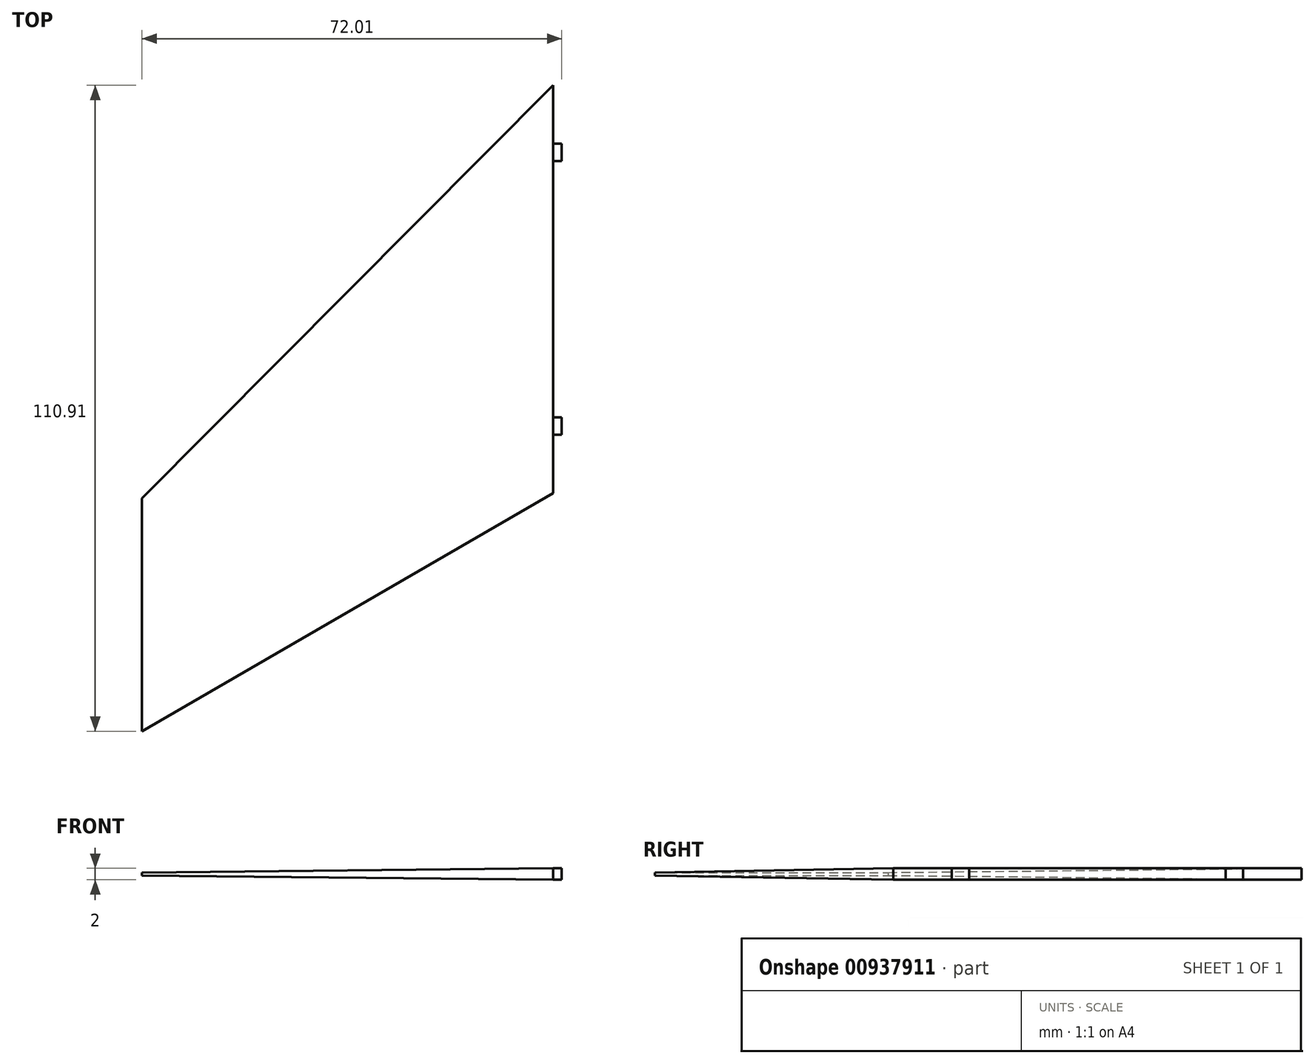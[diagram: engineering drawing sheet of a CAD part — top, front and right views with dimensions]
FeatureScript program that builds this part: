
annotation { "Feature Type Name" : "Feature", "Feature Type Description" : "" }
export const myFeature = defineFeature(function(context is Context, id is Id, definition is map)
    precondition{}
    {
        {
            var Q0;
            Q0=qCreatedBy(makeId("Top.planeOp"),FACE);
            var sketch = newSketch(context, id + "F0", { "sketchPlane" : qUnion([Q0])});
            skLineSegment(sketch, "E0", {"start": v(0, 0) * mm, "end": v(0, 70) * mm});
            skLineSegment(sketch, "E1", {"start": v(0, 70) * mm, "end": v(-70.51, -0.9) * mm});
            skLineSegment(sketch, "E2", {"start": v(-70.51, -0.9) * mm, "end": v(-70.51, -40.9) * mm});
            skLineSegment(sketch, "E3", {"start": v(-70.51, -40.9) * mm, "end": v(0, 0) * mm});
            skSolve(sketch);
        }
        {
            var Q0;
            Q0 = qSketchRegion(id + "F0", true);
            extrude(context, id + "F1", {"entities" : qUnion([Q0]), "depth" : 2 * mm, "offsetDistance" : 25 * mm});
        }
        {
            var Q0;
            Q0=qCreatedBy(makeId("Front.planeOp"),FACE);
            cPlane(context, id + "F2", {"entities" : qUnion([Q0]), "cplaneType" : CPlaneType.OFFSET, "offset" : 89.2 * mm, "oppositeDirection" : true, "width" : 150 * mm, "height" : 150 * mm});
        }
        {
            var Q0;
            Q0=qCreatedBy(id+"F2.planeOp",FACE);
            var sketch = newSketch(context, id + "F3", { "sketchPlane" : qUnion([Q0])});
            skLineSegment(sketch, "E4", {"start": v(0, 0) * mm, "end": v(-70.51, 0.75) * mm});
            skLineSegment(sketch, "E5", {"start": v(-70.51, 0.75) * mm, "end": v(-70.51, 0) * mm});
            skLineSegment(sketch, "E6", {"start": v(-70.51, 0) * mm, "end": v(0, 0) * mm});
            skLineSegment(sketch, "E7", {"start": v(0, 2) * mm, "end": v(-70.51, 1.25) * mm});
            skLineSegment(sketch, "E8", {"start": v(-70.51, 1.25) * mm, "end": v(-70.51, 2) * mm});
            skLineSegment(sketch, "E9", {"start": v(-70.51, 2) * mm, "end": v(0, 2) * mm});
            skSolve(sketch);
        }
        {
            var Q0;
            Q0 = qSketchRegion(id + "F3", true);
            extrude(context, id + "F4", {"entities" : qUnion([Q0]), "operationType" : NewBodyOperationType.REMOVE, "endBound" : BoundingType.THROUGH_ALL, "depth" : 25 * mm, "offsetDistance" : 25 * mm});
        }
        {
            var Q0;
            Q0=makeQuery(id+"F1.opExtrude","SWEPT_FACE",FACE,{"disambiguationData":[OSD([sQuery(id+"F0.wireOp",EDGE,"E0")])]});
            var sketch = newSketch(context, id + "F5", { "sketchPlane" : qUnion([Q0])});
            skLineSegment(sketch, "E10", {"start": v(60, 0) * mm, "end": v(60, 2) * mm});
            skLineSegment(sketch, "E11", {"start": v(60, 2) * mm, "end": v(57, 2) * mm});
            skLineSegment(sketch, "E12", {"start": v(57, 2) * mm, "end": v(57, 0) * mm});
            skLineSegment(sketch, "E13", {"start": v(57, 0) * mm, "end": v(60, 0) * mm});
            skLineSegment(sketch, "E14", {"start": v(13, 0) * mm, "end": v(13, 2) * mm});
            skLineSegment(sketch, "E15", {"start": v(13, 2) * mm, "end": v(10, 2) * mm});
            skLineSegment(sketch, "E16", {"start": v(10, 2) * mm, "end": v(10, 0) * mm});
            skLineSegment(sketch, "E17", {"start": v(10, 0) * mm, "end": v(13, 0) * mm});
            skSolve(sketch);
        }
        {
            var Q0;
            Q0 = qSketchRegion(id + "F5", true);
            extrude(context, id + "F6", {"entities" : qUnion([Q0]), "operationType" : NewBodyOperationType.ADD, "depth" : 1.5 * mm, "offsetDistance" : 25 * mm});
        }
    });
